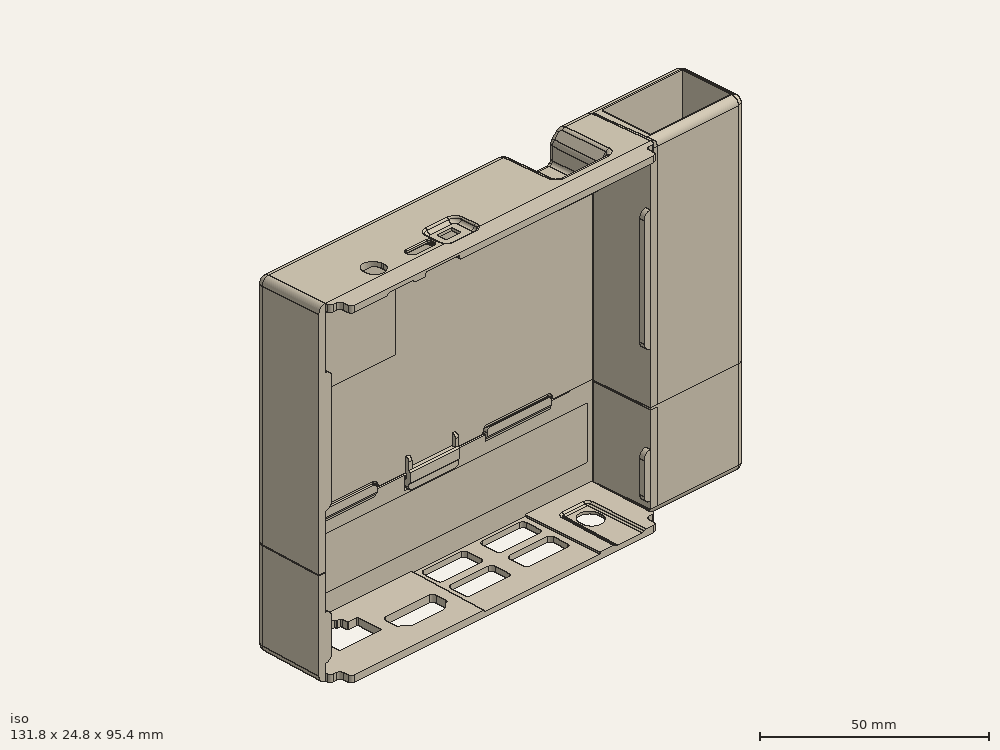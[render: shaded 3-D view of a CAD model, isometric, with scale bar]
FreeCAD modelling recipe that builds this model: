
FCSTD DOCUMENT  (FreeCAD 0.20R29177 +233 (Git))
Label: N2Case_10_12_2022
License: All rights reserved
LicenseURL: http://en.wikipedia.org/wiki/All_rights_reserved
objects: Part::Box×22, Part::Cylinder×11, Part::MultiFuse×9, Part::Cut×9, Part::Sphere×4, Part::Feature×2, Sketcher::SketchObject×2, PartDesign::Pad×2, PartDesign::Body×2
note: 65 computed .brp shape members not serialized (recipe doc carries the construction recipe); baked Part::Feature solids carry a one-line shape summary decoded from their .brp

FEATURE [Part::Feature] Solid  label="N2_BOTTOM_COVER"
  shape: bbox 104.6 x 25.21 x 71.78 mm, 343 faces (baked)
FEATURE [Part::Feature] Solid001  label="N2_TOP_COVER"
  shape: bbox 104.6 x 24.81 x 29.22 mm, 349 faces (baked)
FEATURE [Part::Box] Box  label="Cube"
  AttacherType = Attacher::AttachEngine3D
  Height = 15
  Length = 62.5
  Placement = pos=(-49,18,44) rot=(0,-1,0;4.71239rad)
  Width = 2
FEATURE [Part::MultiFuse] Fusion  label="BottomCover"
  Shapes = -> [Solid,Box]
FEATURE [Part::Box] Box001  label="Cube001"
  AttacherType = Attacher::AttachEngine3D
  Height = 15
  Length = 97.5
  Placement = pos=(48.5,20,-3.5) rot=(0,1,0;3.14159rad)
  Width = 2
FEATURE [Part::Cut] Cut
  Base = -> Fusion
  Tool = -> Box001
FEATURE [Part::Box] Box002  label="usbEthernet"
  AttacherType = Attacher::AttachEngine3D
  Height = 25
  Length = 72
  Placement = pos=(52.5,2.6,47.4) rot=(0,1,0;1.5708rad)
  Width = 15
FEATURE [Part::Box] Box003  label="usbEthernetCover"
  AttacherType = Attacher::AttachEngine3D
  Height = 27.5
  Length = 72
  Placement = pos=(50.5,2.2,47.4) rot=(0,1,0;1.5708rad)
  Width = 15.85
FEATURE [Part::Box] Box004  label="usbEthernetCover001"
  AttacherType = Attacher::AttachEngine3D
  Height = 27.52
  Length = 65.19
  Placement = pos=(49.98,17.6,45.39) rot=(0,1,0;1.5708rad)
  Width = 2.4
FEATURE [Part::Box] Box005  label="usbEthernetCover002"
  AttacherType = Attacher::AttachEngine3D
  Height = 2
  Length = 65.19
  Placement = pos=(77.5,2.2,45.39) rot=(0,1,0;1.5708rad)
  Width = 15.8
FEATURE [Part::Cylinder] Cylinder
  Angle = 90
  AttacherType = Attacher::AttachEngine3D
  FirstAngle = 0
  Height = 65.2
  Placement = pos=(77.5,2.2,-19.8) rot=(0,0,1;4.71239rad)
  Radius = 2
  SecondAngle = 0
FEATURE [Part::Cylinder] Cylinder001
  Angle = 90
  AttacherType = Attacher::AttachEngine3D
  FirstAngle = 0
  Height = 27.5
  Placement = pos=(77.5,18,45.4) rot=(0,1,0;4.71239rad)
  Radius = 2
  SecondAngle = 0
FEATURE [Part::Cylinder] Cylinder002
  Angle = 90
  AttacherType = Attacher::AttachEngine3D
  FirstAngle = 0
  Height = 15.8
  Placement = pos=(77.5,2.2,45.4) rot=(0.57735,0.57735,0.57735;4.18879rad)
  Radius = 2
  SecondAngle = 0
FEATURE [Part::Cylinder] Cylinder003
  Angle = 90
  AttacherType = Attacher::AttachEngine3D
  FirstAngle = 0
  Height = 65.2
  Placement = pos=(77.5,18,-19.8) rot=(0,0,1;0rad)
  Radius = 2
  SecondAngle = 0
FEATURE [Part::Box] Box006  label="usbEthernetCover003"
  AttacherType = Attacher::AttachEngine3D
  Height = 27.2
  Length = 65.19
  Placement = pos=(50.3,0.2,45.39) rot=(0,1,0;1.5708rad)
  Width = 2.4
FEATURE [Part::Cylinder] Cylinder004
  Angle = 90
  AttacherType = Attacher::AttachEngine3D
  FirstAngle = 0
  Height = 26.4
  Placement = pos=(77.5,2.2,45.4) rot=(-0.57735,0.57735,0.57735;4.18879rad)
  Radius = 2
  SecondAngle = 0
FEATURE [Part::Sphere] Sphere
  Angle1 = -90
  Angle2 = 90
  Angle3 = 360
  AttacherType = Attacher::AttachEngine3D
  Placement = pos=(77.5,18,45.4) rot=(0,0,1;0rad)
  Radius = 2
FEATURE [Part::Sphere] Sphere001
  Angle1 = -90
  Angle2 = 90
  Angle3 = 360
  AttacherType = Attacher::AttachEngine3D
  Placement = pos=(77.5,2.2,45.4) rot=(0,0,1;0rad)
  Radius = 2
FEATURE [Part::MultiFuse] Fusion001  label="usbCover"
  Shapes = -> [Box003,Box004,Box005,Cylinder,Cylinder001,Cylinder002,Cylinder003,Box006,Cylinder004,Sphere,Sphere001]
FEATURE [Part::MultiFuse] Fusion002
  Shapes = -> [Cut,Fusion001]
FEATURE [Part::Cut] Cut001  label="front"
  Base = -> Fusion002
  Tool = -> Box002
FEATURE [Part::Box] Box007  label="Cube002"
  AttacherType = Attacher::AttachEngine3D
  Height = 10
  Length = 30
  Placement = pos=(79.5,0,-19.8) rot=(0,1,0;3.14159rad)
  Width = 20
FEATURE [Part::Cut] Cut002
  Base = -> Cut001
  Tool = -> Box007
FEATURE [Part::Box] Box008  label="Cube003"
  AttacherType = Attacher::AttachEngine3D
  Height = 10
  Length = 30
  Placement = pos=(79.5,0,-19.8) rot=(0,1,0;3.14159rad)
  Width = 20
FEATURE [Part::Cut] Cut003  label="front001"
  Base = -> Cut002
  Tool = -> Box008
FEATURE [Part::Box] Box009  label="usbEthernet001"
  AttacherType = Attacher::AttachEngine3D
  Height = 25
  Length = 72
  Placement = pos=(52.5,2.6,6.3) rot=(0,1,0;1.5708rad)
  Width = 15
FEATURE [Part::Box] Box010  label="usbEthernetCover004"
  AttacherType = Attacher::AttachEngine3D
  Height = 27.5
  Length = 72
  Placement = pos=(50.5,2.2,-19.8) rot=(0,1,0;1.5708rad)
  Width = 15.85
FEATURE [Part::Box] Box011  label="usbEthernetCover005"
  AttacherType = Attacher::AttachEngine3D
  Height = 27.52
  Length = 65.19
  Placement = pos=(49.98,17.6,-19.8) rot=(0,1,0;1.5708rad)
  Width = 2.4
FEATURE [Part::Box] Box012  label="usbEthernetCover006"
  AttacherType = Attacher::AttachEngine3D
  Height = 2
  Length = 65.19
  Placement = pos=(77.5,2.2,-19.8) rot=(0,1,0;1.5708rad)
  Width = 15.8
FEATURE [Part::Box] Box013  label="usbEthernetCover007"
  AttacherType = Attacher::AttachEngine3D
  Height = 27.2
  Length = 65.19
  Placement = pos=(50.3,0.2,-19.8) rot=(0,1,0;1.5708rad)
  Width = 2.4
FEATURE [Part::Box] Box016  label="Cube005"
  AttacherType = Attacher::AttachEngine3D
  Height = 50
  Length = 29.5
  Placement = pos=(79.5,0,-45.4) rot=(0,1,0;3.14159rad)
  Width = 20
FEATURE [Part::MultiFuse] Fusion003
  Shapes = -> [Solid001,Box010,Box011,Box012,Box013]
FEATURE [Part::Cut] Cut004
  Base = -> Fusion003
  Tool = -> Box016
FEATURE [Part::Cut] Cut005
  Base = -> Cut004
  Tool = -> Box009
FEATURE [Part::Box] Box017  label="Cube006"
  AttacherType = Attacher::AttachEngine3D
  Height = 50
  Length = 23.5
  Placement = pos=(73.4,17.6,-45.39) rot=(0,1,0;3.14159rad)
  Width = 20
FEATURE [Part::Cut] Cut006
  Base = -> Cut005
  Tool = -> Box017
FEATURE [Part::Cylinder] Cylinder005
  Angle = 90
  AttacherType = Attacher::AttachEngine3D
  FirstAngle = 0
  Height = 65.2
  Placement = pos=(77.5,2.2,-45.4) rot=(0,0,-1;1.5708rad)
  Radius = 2
  SecondAngle = 0
FEATURE [Part::Cylinder] Cylinder006
  Angle = 90
  AttacherType = Attacher::AttachEngine3D
  FirstAngle = 0
  Height = 27.5
  Placement = pos=(77.5,18,-45.4) rot=(0,-1,0;1.5708rad)
  Radius = 2
  SecondAngle = 0
FEATURE [Part::Cylinder] Cylinder007
  Angle = 90
  AttacherType = Attacher::AttachEngine3D
  FirstAngle = 0
  Height = 15.8
  Placement = pos=(77.5,2.2,-45.4) rot=(-1,0,0;1.5708rad)
  Radius = 2
  SecondAngle = 0
FEATURE [Part::Cylinder] Cylinder008
  Angle = 90
  AttacherType = Attacher::AttachEngine3D
  FirstAngle = 0
  Height = 65.2
  Placement = pos=(77.5,18,-45.4) rot=(0,0,1;0rad)
  Radius = 2
  SecondAngle = 0
FEATURE [Part::Cylinder] Cylinder009
  Angle = 90
  AttacherType = Attacher::AttachEngine3D
  FirstAngle = 0
  Height = 27.6
  Placement = pos=(77.5,2.2,-45.4) rot=(-0.707107,0,0.707107;3.14159rad)
  Radius = 2
  SecondAngle = 0
FEATURE [Part::Cylinder] Cylinder010
  Angle = 90
  AttacherType = Attacher::AttachEngine3D
  FirstAngle = 0
  Height = 27.6
  Placement = pos=(77.5,18,-45.4) rot=(-0.57735,-0.57735,0.57735;2.0944rad)
  Radius = 2
  SecondAngle = 0
FEATURE [Part::Box] Box018  label="Cube007"
  AttacherType = Attacher::AttachEngine3D
  Height = 2
  Length = 27.6
  Placement = pos=(49.9,18,-45.4) rot=(1,0,0;3.14159rad)
  Width = 15.8
FEATURE [Part::Box] Box019  label="usbEthernet002"
  AttacherType = Attacher::AttachEngine3D
  Height = 25
  Length = 72
  Placement = pos=(52.5,2.6,-2.5) rot=(0,1,0;1.5708rad)
  Width = 15
FEATURE [Part::Sphere] Sphere002
  Angle1 = -90
  Angle2 = 90
  Angle3 = 360
  AttacherType = Attacher::AttachEngine3D
  Placement = pos=(77.5,18,-45.4) rot=(0,0,1;0rad)
  Radius = 2
FEATURE [Part::Sphere] Sphere003
  Angle1 = -90
  Angle2 = 90
  Angle3 = 360
  AttacherType = Attacher::AttachEngine3D
  Placement = pos=(77.5,2.2,-45.4) rot=(0,0,1;0rad)
  Radius = 2
FEATURE [Part::Box] Box020  label="Cube008"
  AttacherType = Attacher::AttachEngine3D
  Height = 40
  Length = 10
  Placement = pos=(73.6,0,-19.8) rot=(0,0,1;0rad)
  Width = 22
FEATURE [Part::MultiFuse] Fusion004  label="cuts"
  Shapes = -> [Box020,Box019]
FEATURE [Part::MultiFuse] Fusion005
  Shapes = -> [Sphere003,Cut006,Cylinder005,Cylinder006,Cylinder007,Cylinder008,Cylinder009,Cylinder010,Box018,Sphere002]
FEATURE [Part::Cut] Cut007  label="back"
  Base = -> Fusion005
  Tool = -> Fusion004
FEATURE [Part::Box] Box021  label="Cube009"
  AttacherType = Attacher::AttachEngine3D
  Height = 15
  Length = 97.5
  Placement = pos=(48.5,18,-25.1) rot=(0,1,0;3.14159rad)
  Width = 2
FEATURE [Part::MultiFuse] Fusion006  label="back001"
  Shapes = -> [Cut007,Box021]
FEATURE [Part::Box] Box068  label="logoBase001"
  AttacherType = Attacher::AttachEngine3D
  Height = 30
  Length = 35
  Placement = pos=(21.5,-44,15.25) rot=(0,0,1;0rad)
  Width = 1.8
FEATURE [Sketcher::SketchObject] Sketch001
  FullyConstrained = false
  MapMode = 5
  Support = -> [XY_Plane001]
  sketch-geometry (205):
    g0: LineSegment StartX=-15.0667 StartY=-2.9879 StartZ=0 EndX=-14.4175 EndY=-3.20194 EndZ=0
    g1: LineSegment StartX=-14.1386 StartY=-3.3581 StartZ=0 EndX=-13.8673 EndY=-3.55064 EndZ=0
    g2: LineSegment StartX=-10.8098 StartY=-4.00788 StartZ=0 EndX=-10.5716 EndY=-4.29909 EndZ=0
    g3: LineSegment StartX=-10.5716 StartY=-4.29909 StartZ=0 EndX=-10.1338 EndY=-4.33136 EndZ=0
    g4: LineSegment StartX=-10.1338 StartY=-4.33136 StartZ=0 EndX=-9.89036 EndY=-4.3898 EndZ=0
    g5: LineSegment StartX=-9.51656 StartY=-5.73022 StartZ=0 EndX=-9.24931 EndY=-5.76229 EndZ=0
    g6: LineSegment StartX=-9.24931 StartY=-5.76229 StartZ=0 EndX=-8.92861 EndY=-5.90126 EndZ=0
    g7: LineSegment StartX=-8.92861 StartY=-5.90126 StartZ=0 EndX=-8.54378 EndY=-5.86384 EndZ=0
    g8: LineSegment StartX=-8.54378 StartY=-5.86384 StartZ=0 EndX=-7.71788 EndY=-5.75845 EndZ=0
    g9: LineSegment StartX=-7.71788 StartY=-5.75845 StartZ=0 EndX=-7.37291 EndY=-5.97257 EndZ=0
    g10: LineSegment StartX=-7.37291 StartY=-5.97257 StartZ=0 EndX=-6.72487 EndY=-5.72038 EndZ=0
    g11: LineSegment StartX=-6.72487 StartY=-5.72038 StartZ=0 EndX=-6.27066 EndY=-5.69481 EndZ=0
    g12: LineSegment StartX=-6.27066 StartY=-5.69481 StartZ=0 EndX=-6.06223 EndY=-5.80493 EndZ=0
    g13: LineSegment StartX=-6.06223 StartY=-5.80493 StartZ=0 EndX=-5.35089 EndY=-5.48914 EndZ=0
    g14: LineSegment StartX=-5.35089 StartY=-5.48914 StartZ=0 EndX=-5.02402 EndY=-5.48914 EndZ=0
    g15: LineSegment StartX=-5.02402 StartY=-5.48914 StartZ=0 EndX=-4.80126 EndY=-5.53132 EndZ=0
    g16: LineSegment StartX=-4.80126 StartY=-5.53132 StartZ=0 EndX=-4.19735 EndY=-5.16248 EndZ=0
    g17: LineSegment StartX=-3.75191 StartY=-4.97251 StartZ=0 EndX=-3.37714 EndY=-4.97251 EndZ=0
    g18: LineSegment StartX=-3.37714 StartY=-4.97251 StartZ=0 EndX=-2.81898 EndY=-4.45422 EndZ=0
    g19: LineSegment StartX=-2.81898 StartY=-4.45422 StartZ=0 EndX=-2.62761 EndY=-4.34259 EndZ=0
    g20: LineSegment StartX=-2.62761 StartY=-4.34259 StartZ=0 EndX=-2.15112 EndY=-4.35765 EndZ=0
    g21: LineSegment StartX=-2.38042 StartY=-4.51801 StartZ=0 EndX=-3.18577 EndY=-5.42702 EndZ=0
    g22: LineSegment StartX=-3.18577 StartY=-5.42702 StartZ=0 EndX=-3.61318 EndY=-6.05824 EndZ=0
    g23: LineSegment StartX=-3.61318 StartY=-6.05824 StartZ=0 EndX=-3.7111 EndY=-6.64579 EndZ=0
    g24: LineSegment StartX=-3.7111 StartY=-6.64579 StartZ=0 EndX=-3.83514 EndY=-7.15501 EndZ=0
    g25: LineSegment StartX=-3.83514 StartY=-7.15501 StartZ=0 EndX=-3.75878 EndY=-7.50876 EndZ=0
    g26: LineSegment StartX=-3.75878 StartY=-7.50876 StartZ=0 EndX=-3.70596 EndY=-7.68135 EndZ=0
    g27: LineSegment StartX=-3.70596 StartY=-7.68135 StartZ=0 EndX=-3.53967 EndY=-7.85202 EndZ=0
    g28: LineSegment StartX=-3.53967 StartY=-7.85202 StartZ=0 EndX=-3.4685 EndY=-8.65617 EndZ=0
    g29: LineSegment StartX=-3.27268 StartY=-8.56671 StartZ=0 EndX=-3.16823 EndY=-8.76909 EndZ=0
    g30: LineSegment StartX=-3.07088 StartY=-9.32083 StartZ=0 EndX=-2.84207 EndY=-9.3355 EndZ=0
    g31: LineSegment StartX=-2.84207 StartY=-9.3355 StartZ=0 EndX=-2.45193 EndY=-10.0982 EndZ=0
    g32: LineSegment StartX=-2.45193 StartY=-10.0982 StartZ=0 EndX=-2.24953 EndY=-10.1304 EndZ=0
    g33: LineSegment StartX=-2.24953 StartY=-10.1304 StartZ=0 EndX=-0.96042 EndY=-11.8753 EndZ=0
    g34: LineSegment StartX=-0.96042 StartY=-11.8753 StartZ=0 EndX=-0.153326 EndY=-11.3889 EndZ=0
    g35: LineSegment StartX=-0.153326 StartY=-11.3889 StartZ=0 EndX=0.461347 EndY=-10.7689 EndZ=0
    g36: LineSegment StartX=0.461347 StartY=-10.7689 StartZ=0 EndX=0.669802 EndY=-10.7261 EndZ=0
    g37: LineSegment StartX=0.669802 StartY=-10.7261 StartZ=0 EndX=1.31724 EndY=-9.70998 EndZ=0
    g38: LineSegment StartX=1.31724 StartY=-9.70998 StartZ=0 EndX=1.51826 EndY=-9.65081 EndZ=0
    g39: LineSegment StartX=1.51826 StartY=-9.65081 StartZ=0 EndX=1.74022 EndY=-9.08937 EndZ=0
    g40: LineSegment StartX=1.74022 StartY=-9.08937 StartZ=0 EndX=2.02094 EndY=-9.04367 EndZ=0
    g41: LineSegment StartX=2.02094 StartY=-9.04367 StartZ=0 EndX=2.39306 EndY=-7.80327 EndZ=0
    g42: LineSegment StartX=2.39306 StartY=-7.80327 StartZ=0 EndX=2.58839 EndY=-7.69871 EndZ=0
    g43: LineSegment StartX=2.6542 StartY=-7.03945 StartZ=0 EndX=2.86963 EndY=-6.81749 EndZ=0
    g44: LineSegment StartX=2.86963 StartY=-6.81749 StartZ=0 EndX=3.0916 EndY=-6.92847 EndZ=0
    g45: LineSegment StartX=3.0916 StartY=-6.92847 StartZ=0 EndX=3.79666 EndY=-7.57478 EndZ=0
    g46: LineSegment StartX=3.79666 StartY=-7.57478 StartZ=0 EndX=3.93376 EndY=-7.50297 EndZ=0
    g47: LineSegment StartX=3.93376 StartY=-7.50297 StartZ=0 EndX=4.46256 EndY=-7.97301 EndZ=0
    g48: LineSegment StartX=4.46256 StartY=-7.97301 StartZ=0 EndX=4.68452 EndY=-7.92079 EndZ=0
    g49: LineSegment StartX=4.68452 StartY=-7.92079 StartZ=0 EndX=5.1154 EndY=-8.34513 EndZ=0
    g50: LineSegment StartX=5.1154 StartY=-8.34513 StartZ=0 EndX=5.32431 EndY=-8.28637 EndZ=0
    g51: LineSegment StartX=5.32431 StartY=-8.28637 StartZ=0 EndX=6.23668 EndY=-8.79564 EndZ=0
    g52: LineSegment StartX=6.23668 StartY=-8.79564 StartZ=0 EndX=6.50362 EndY=-8.76631 EndZ=0
    g53: LineSegment StartX=6.50362 StartY=-8.76631 StartZ=0 EndX=7.14802 EndY=-9.05537 EndZ=0
    g54: LineSegment StartX=7.14802 StartY=-9.05537 StartZ=0 EndX=8.04883 EndY=-9.18613 EndZ=0
    g55: LineSegment StartX=8.04883 StartY=-9.18613 StartZ=0 EndX=8.36847 EndY=-7.93662 EndZ=0
    g56: LineSegment StartX=8.36847 StartY=-7.93662 StartZ=0 EndX=8.49923 EndY=-7.79133 EndZ=0
    g57: LineSegment StartX=8.49923 StartY=-7.79133 StartZ=0 EndX=8.43477 EndY=-6.72206 EndZ=0
    g58: LineSegment StartX=8.43477 StartY=-6.72206 StartZ=0 EndX=8.58621 EndY=-6.47988 EndZ=0
    g59: LineSegment StartX=8.58621 StartY=-6.47988 StartZ=0 EndX=8.32296 EndY=-5.53178 EndZ=0
    g60: LineSegment StartX=8.32296 StartY=-5.53178 StartZ=0 EndX=8.43984 EndY=-5.19091 EndZ=0
    g61: LineSegment StartX=8.43984 StartY=-5.19091 StartZ=0 EndX=8.07426 EndY=-4.39307 EndZ=0
    g62: LineSegment StartX=8.07426 StartY=-4.39307 StartZ=0 EndX=8.04236 EndY=-4.17777 EndZ=0
    g63: LineSegment StartX=8.04236 StartY=-4.17777 StartZ=0 EndX=8.0902 EndY=-3.99438 EndZ=0
    g64: LineSegment StartX=8.4103 StartY=-4.11103 StartZ=0 EndX=8.72013 EndY=-4.0502 EndZ=0
    g65: LineSegment StartX=8.72013 StartY=-4.0502 StartZ=0 EndX=9.31817 EndY=-4.0502 EndZ=0
    g66: LineSegment StartX=9.31817 StartY=-4.0502 StartZ=0 EndX=9.82964 EndY=-4.15887 EndZ=0
    g67: LineSegment StartX=10.1326 StartY=-3.9675 StartZ=0 EndX=10.5175 EndY=-3.9623 EndZ=0
    g68: LineSegment StartX=10.5175 StartY=-3.9623 StartZ=0 EndX=10.8831 EndY=-3.97536 EndZ=0
    g69: LineSegment StartX=10.8831 StartY=-3.97536 StartZ=0 EndX=11.2245 EndY=-4.09431 EndZ=0
    g70: LineSegment StartX=11.2245 StartY=-4.09431 StartZ=0 EndX=11.6861 EndY=-3.91007 EndZ=0
    g71: LineSegment StartX=11.6861 StartY=-3.91007 StartZ=0 EndX=12.1039 EndY=-3.88396 EndZ=0
    g72: LineSegment StartX=12.1039 StartY=-3.88396 StartZ=0 EndX=12.6 EndY=-3.9623 EndZ=0
    g73: LineSegment StartX=12.6 StartY=-3.9623 StartZ=0 EndX=13.5793 EndY=-3.87743 EndZ=0
    g74: LineSegment StartX=13.5793 StartY=-3.87743 StartZ=0 EndX=14.3888 EndY=-3.74687 EndZ=0
    g75: LineSegment StartX=14.3888 StartY=-3.74687 StartZ=0 EndX=14.7544 EndY=-3.68158 EndZ=0
    g76: LineSegment StartX=14.7544 StartY=-3.68158 StartZ=0 EndX=15.2767 EndY=-3.75339 EndZ=0
    g77: LineSegment StartX=15.2767 StartY=-3.75339 StartZ=0 EndX=15.0432 EndY=-3.24137 EndZ=0
    g78: LineSegment StartX=15.0432 StartY=-3.24137 StartZ=0 EndX=14.5209 EndY=-2.51672 EndZ=0
    g79: LineSegment StartX=14.5209 StartY=-2.51672 StartZ=0 EndX=14.0378 EndY=-1.99445 EndZ=0
    g80: LineSegment StartX=14.0378 StartY=-1.99445 StartZ=0 EndX=13.2802 EndY=-1.54625 EndZ=0
    g81: LineSegment StartX=13.2802 StartY=-1.54625 StartZ=0 EndX=13.0438 EndY=-1.23117 EndZ=0
    g82: LineSegment StartX=13.0438 StartY=-1.23117 StartZ=0 EndX=12.1074 EndY=-0.797939 EndZ=0
    g83: LineSegment StartX=12.1074 StartY=-0.797939 StartZ=0 EndX=11.3804 EndY=-0.250878 EndZ=0
    g84: LineSegment StartX=11.3804 StartY=-0.250878 StartZ=0 EndX=10.4396 EndY=0.304889 EndZ=0
    g85: LineSegment StartX=10.4396 StartY=0.304889 StartZ=0 EndX=9.59526 EndY=0.727998 EndZ=0
    g86: LineSegment StartX=9.59526 StartY=0.727998 StartZ=0 EndX=8.53624 EndY=0.97306 EndZ=0
    g87: LineSegment StartX=8.53624 StartY=0.97306 StartZ=0 EndX=7.199 EndY=0.97306 EndZ=0
    g88: LineSegment StartX=7.199 StartY=0.97306 StartZ=0 EndX=5.77932 EndY=0.795578 EndZ=0
    g89: LineSegment StartX=5.77932 StartY=0.795578 StartZ=0 EndX=5.60186 EndY=0.795578 EndZ=0
    g90: LineSegment StartX=5.60186 StartY=0.795578 StartZ=0 EndX=5.83178 EndY=0.981815 EndZ=0
    g91: LineSegment StartX=5.83178 StartY=0.981815 StartZ=0 EndX=6.25403 EndY=1.1582 EndZ=0
    g92: LineSegment StartX=6.30214 StartY=1.38269 StartZ=0 EndX=7.17987 EndY=1.70686 EndZ=0
    g93: LineSegment StartX=7.17987 StartY=1.70686 StartZ=0 EndX=7.44682 EndY=1.79438 EndZ=0
    g94: LineSegment StartX=7.44682 StartY=1.79438 StartZ=0 EndX=7.49058 EndY=2.12696 EndZ=0
    g95: LineSegment StartX=7.49058 StartY=2.12696 StartZ=0 EndX=8.30058 EndY=2.66839 EndZ=0
    g96: LineSegment StartX=8.30058 StartY=2.66839 StartZ=0 EndX=8.68575 EndY=2.81854 EndZ=0
    g97: LineSegment StartX=8.68575 StartY=2.81854 StartZ=0 EndX=8.68575 EndY=3.12537 EndZ=0
    g98: LineSegment StartX=8.68575 StartY=3.12537 StartZ=0 EndX=8.89508 EndY=3.18684 EndZ=0
    g99: LineSegment StartX=8.89508 StartY=3.18684 StartZ=0 EndX=9.63492 EndY=4.06602 EndZ=0
    g100: LineSegment StartX=9.63492 StartY=4.06602 StartZ=0 EndX=9.62638 EndY=4.32743 EndZ=0
    g101: LineSegment StartX=9.62638 StartY=4.32743 StartZ=0 EndX=10.2068 EndY=5.18314 EndZ=0
    g102: LineSegment StartX=10.2068 StartY=5.18314 StartZ=0 EndX=9.25518 EndY=5.64445 EndZ=0
    g103: LineSegment StartX=9.1102 StartY=5.87597 StartZ=0 EndX=8.32132 EndY=5.97336 EndZ=0
    g104: LineSegment StartX=8.32132 StartY=5.97336 StartZ=0 EndX=8.15466 EndY=6.06625 EndZ=0
    g105: LineSegment StartX=7.63471 StartY=6.13088 StartZ=0 EndX=7.56391 EndY=6.33267 EndZ=0
    g106: LineSegment StartX=7.56391 StartY=6.33267 StartZ=0 EndX=6.74832 EndY=6.35496 EndZ=0
    g107: LineSegment StartX=6.74832 StartY=6.35496 StartZ=0 EndX=6.46819 EndY=6.29526 EndZ=0
    g108: LineSegment StartX=6.46819 StartY=6.29526 StartZ=0 EndX=6.27042 EndY=6.61061 EndZ=0
    g109: LineSegment StartX=6.27042 StartY=6.61061 StartZ=0 EndX=5.40453 EndY=6.33267 EndZ=0
    g110: LineSegment StartX=5.40453 StartY=6.33267 StartZ=0 EndX=5.27091 EndY=6.47164 EndZ=0
    g111: LineSegment StartX=5.27091 StartY=6.47164 StartZ=0 EndX=4.56942 EndY=6.24725 EndZ=0
    g112: LineSegment StartX=4.56942 StartY=6.24725 StartZ=0 EndX=4.44161 EndY=6.40652 EndZ=0
    g113: LineSegment StartX=4.44161 StartY=6.40652 StartZ=0 EndX=3.4195 EndY=5.94588 EndZ=0
    g114: LineSegment StartX=3.4195 StartY=5.94588 StartZ=0 EndX=3.29192 EndY=6.1532 EndZ=0
    g115: LineSegment StartX=3.29192 StartY=6.1532 StartZ=0 EndX=2.15964 EndY=5.49137 EndZ=0
    g116: LineSegment StartX=2.15964 StartY=5.49137 StartZ=0 EndX=2.00016 EndY=5.69869 EndZ=0
    g117: LineSegment StartX=2.00016 StartY=5.69869 StartZ=0 EndX=1.6185 EndY=5.34828 EndZ=0
    g118: LineSegment StartX=1.6185 StartY=5.34828 StartZ=0 EndX=1.45984 EndY=5.94974 EndZ=0
    g119: LineSegment StartX=1.38165 StartY=6.28651 StartZ=0 EndX=1.14534 EndY=6.29963 EndZ=0
    g120: LineSegment StartX=0.348522 StartY=7.29544 StartZ=0 EndX=0.126706 EndY=7.68126 EndZ=0
    g121: LineSegment StartX=0.126706 StartY=7.68126 StartZ=0 EndX=-0.415308 EndY=8.18163 EndZ=0
    g122: LineSegment StartX=-0.415308 StartY=8.18163 StartZ=0 EndX=-0.872658 EndY=8.6237 EndZ=0
    g123: LineSegment StartX=-0.872658 StartY=8.6237 StartZ=0 EndX=-1.12074 EndY=8.64329 EndZ=0
    g124: LineSegment StartX=-1.12074 StartY=8.64329 StartZ=0 EndX=-1.79316 EndY=9.11986 EndZ=0
    g125: LineSegment StartX=-1.79316 StartY=9.11986 StartZ=0 EndX=-2.31488 EndY=9.12122 EndZ=0
    g126: LineSegment StartX=-2.31488 StartY=9.12122 StartZ=0 EndX=-2.71321 EndY=9.13846 EndZ=0
    g127: LineSegment StartX=-2.71321 StartY=9.13846 StartZ=0 EndX=-2.88425 EndY=9.34157 EndZ=0
    g128: LineSegment StartX=-2.88425 StartY=9.34157 StartZ=0 EndX=-3.16779 EndY=9.26454 EndZ=0
    g129: LineSegment StartX=-3.70739 StartY=9.82796 StartZ=0 EndX=-4.04915 EndY=9.7003 EndZ=0
    g130: LineSegment StartX=-4.04915 StartY=9.7003 StartZ=0 EndX=-4.42988 EndY=10.011 EndZ=0
    g131: LineSegment StartX=-5.98947 StartY=10.3656 StartZ=0 EndX=-7.32605 EndY=10.4108 EndZ=0
    g132: LineSegment StartX=-7.25254 StartY=9.13254 StartZ=0 EndX=-7.36878 EndY=8.7693 EndZ=0
    g133: LineSegment StartX=-7.36878 StartY=8.7693 StartZ=0 EndX=-7.2614 EndY=7.83762 EndZ=0
    g134: LineSegment StartX=-7.2614 StartY=7.83762 StartZ=0 EndX=-7.41112 EndY=7.6042 EndZ=0
    g135: LineSegment StartX=-7.41112 StartY=7.6042 StartZ=0 EndX=-7.09216 EndY=6.74302 EndZ=0
    g136: LineSegment StartX=-7.09216 StartY=6.74302 StartZ=0 EndX=-7.10014 EndY=6.55962 EndZ=0
    g137: LineSegment StartX=-7.10014 StartY=6.55962 StartZ=0 EndX=-7.29151 EndY=6.3842 EndZ=0
    g138: LineSegment StartX=-7.29151 StartY=6.3842 StartZ=0 EndX=-6.74132 EndY=5.29976 EndZ=0
    g139: LineSegment StartX=-6.74132 StartY=5.29976 StartZ=0 EndX=-6.87495 EndY=5.02732 EndZ=0
    g140: LineSegment StartX=-6.87495 StartY=5.02732 StartZ=0 EndX=-6.31586 EndY=4.42065 EndZ=0
    g141: LineSegment StartX=-6.31586 StartY=4.42065 StartZ=0 EndX=-6.30396 EndY=4.19463 EndZ=0
    g142: LineSegment StartX=-6.30396 StartY=4.19463 StartZ=0 EndX=-6.05415 EndY=4.0043 EndZ=0
    g143: LineSegment StartX=-6.05415 StartY=4.0043 StartZ=0 EndX=-6.18501 EndY=3.95672 EndZ=0
    g144: LineSegment StartX=-6.18501 StartY=3.95672 StartZ=0 EndX=-5.54265 EndY=3.07645 EndZ=0
    g145: LineSegment StartX=-5.54265 StartY=3.07645 StartZ=0 EndX=-5.57833 EndY=2.90991 EndZ=0
    g146: LineSegment StartX=-5.57833 StartY=2.90991 StartZ=0 EndX=-5.1263 EndY=2.41029 EndZ=0
    g147: LineSegment StartX=-5.1263 StartY=2.41029 StartZ=0 EndX=-5.18578 EndY=2.26755 EndZ=0
    g148: LineSegment StartX=-5.18578 StartY=2.26755 StartZ=0 EndX=-4.73375 EndY=1.89878 EndZ=0
    g149: LineSegment StartX=-4.73375 StartY=1.89878 StartZ=0 EndX=-4.42446 EndY=1.5895 EndZ=0
    g150: LineSegment StartX=-4.42446 StartY=1.5895 StartZ=0 EndX=-5.31663 EndY=1.29211 EndZ=0
    g151: LineSegment StartX=-5.31663 StartY=1.29211 StartZ=0 EndX=-5.84004 EndY=1.08988 EndZ=0
    g152: LineSegment StartX=-5.84004 StartY=1.08988 StartZ=0 EndX=-6.04226 EndY=0.792495 EndZ=0
    g153: LineSegment StartX=-6.04226 StartY=0.792495 StartZ=0 EndX=-6.94632 EndY=0.994719 EndZ=0
    g154: LineSegment StartX=-6.94632 StartY=0.994719 StartZ=0 EndX=-7.19613 EndY=0.887659 EndZ=0
    g155: LineSegment StartX=-7.19613 StartY=0.887659 StartZ=0 EndX=-7.8147 EndY=1.0423 EndZ=0
    g156: LineSegment StartX=-7.8147 StartY=1.0423 StartZ=0 EndX=-8.02502 EndY=0.969153 EndZ=0
    g157: LineSegment StartX=-8.02502 StartY=0.969153 StartZ=0 EndX=-8.60267 EndY=1.03042 EndZ=0
    g158: LineSegment StartX=-8.60267 StartY=1.03042 StartZ=0 EndX=-8.8346 EndY=0.872878 EndZ=0
    g159: LineSegment StartX=-8.8346 StartY=0.872878 StartZ=0 EndX=-9.33349 EndY=0.929767 EndZ=0
    g160: LineSegment StartX=-9.33349 StartY=0.929767 StartZ=0 EndX=-9.66169 EndY=0.649695 EndZ=0
    g161: LineSegment StartX=-9.66169 StartY=0.649695 StartZ=0 EndX=-10.3249 EndY=0.649695 EndZ=0
    g162: LineSegment StartX=-10.3249 StartY=0.649695 StartZ=0 EndX=-11.0107 EndY=0.32425 EndZ=0
    g163: LineSegment StartX=-11.0107 StartY=0.32425 StartZ=0 EndX=-11.7283 EndY=0.053139 EndZ=0
    g164: LineSegment StartX=-11.7283 StartY=0.053139 StartZ=0 EndX=-12.2971 EndY=-0.13161 EndZ=0
    g165: LineSegment StartX=-12.2971 StartY=-0.13161 StartZ=0 EndX=-12.4212 EndY=-0.347049 EndZ=0
    g166: LineSegment StartX=-12.4212 StartY=-0.347049 StartZ=0 EndX=-13.296 EndY=-0.817096 EndZ=0
    g167: LineSegment StartX=-13.296 StartY=-0.817096 StartZ=0 EndX=-13.9227 EndY=-1.24144 EndZ=0
    g168: LineSegment StartX=-13.9227 StartY=-1.24144 StartZ=0 EndX=-14.1708 EndY=-1.59398 EndZ=0
    g169: LineSegment StartX=-14.1708 StartY=-1.59398 StartZ=0 EndX=-14.5386 EndY=-2.09216 EndZ=0
    g170: LineSegment StartX=-14.5386 StartY=-2.09216 StartZ=0 EndX=-14.7831 EndY=-2.4577 EndZ=0
    g171: LineSegment StartX=-14.7831 StartY=-2.4577 StartZ=0 EndX=-15.0667 EndY=-2.9879 EndZ=0
    g172: LineSegment StartX=7.82861 StartY=6.04487 StartZ=0 EndX=7.63471 EndY=6.13088 EndZ=0
    g173: LineSegment StartX=-14.4175 StartY=-3.20194 StartZ=0 EndX=-14.1386 EndY=-3.3581 EndZ=0
    g174: LineSegment StartX=-13.8673 StartY=-3.55064 StartZ=0 EndX=-13.4107 EndY=-3.57136 EndZ=0
    g175: LineSegment StartX=-13.1321 StartY=-3.61699 StartZ=0 EndX=-12.817 EndY=-3.62343 EndZ=0
    g176: LineSegment StartX=-12.817 StartY=-3.62343 StartZ=0 EndX=-12.4662 EndY=-3.85302 EndZ=0
    g177: LineSegment StartX=-13.4107 StartY=-3.57136 StartZ=0 EndX=-13.1321 EndY=-3.61699 EndZ=0
    g178: LineSegment StartX=-12.4662 StartY=-3.85302 StartZ=0 EndX=-11.8704 EndY=-3.85302 EndZ=0
    g179: LineSegment StartX=-11.8704 StartY=-3.85302 StartZ=0 EndX=-11.5204 EndY=-4.00836 EndZ=0
    g180: LineSegment StartX=-11.5204 StartY=-4.00836 StartZ=0 EndX=-11.1389 EndY=-4.05555 EndZ=0
    g181: LineSegment StartX=-11.1389 StartY=-4.05555 StartZ=0 EndX=-10.8098 EndY=-4.00788 EndZ=0
    g182: LineSegment StartX=-9.89036 StartY=-4.3898 StartZ=0 EndX=-9.99555 EndY=-4.87697 EndZ=0
    g183: LineSegment StartX=-9.99555 StartY=-4.87697 StartZ=0 EndX=-10.0894 EndY=-5.36391 EndZ=0
    g184: LineSegment StartX=-10.0894 StartY=-5.36391 StartZ=0 EndX=-10.107 EndY=-5.50471 EndZ=0
    g185: LineSegment StartX=-10.107 StartY=-5.50471 StartZ=0 EndX=-9.77848 EndY=-5.63965 EndZ=0
    g186: LineSegment StartX=-9.77848 StartY=-5.63965 StartZ=0 EndX=-9.51656 EndY=-5.73022 EndZ=0
    g187: LineSegment StartX=-4.19735 StartY=-5.16248 StartZ=0 EndX=-3.75191 EndY=-4.97251 EndZ=0
    g188: LineSegment StartX=-2.38042 StartY=-4.51801 StartZ=0 EndX=-2.15112 EndY=-4.35765 EndZ=0
    g189: LineSegment StartX=-3.4685 StartY=-8.65617 StartZ=0 EndX=-3.27268 EndY=-8.56671 EndZ=0
    g190: LineSegment StartX=-3.16823 StartY=-8.76909 StartZ=0 EndX=-3.07088 EndY=-9.32083 EndZ=0
    g191: LineSegment StartX=2.58839 StartY=-7.69871 StartZ=0 EndX=2.6542 EndY=-7.03945 EndZ=0
    g192: LineSegment StartX=8.0902 StartY=-3.99438 StartZ=0 EndX=8.4103 EndY=-4.11103 EndZ=0
    g193: LineSegment StartX=9.82964 StartY=-4.15887 StartZ=0 EndX=10.1326 EndY=-3.9675 EndZ=0
    g194: LineSegment StartX=6.30214 StartY=1.38269 StartZ=0 EndX=6.25403 EndY=1.1582 EndZ=0
    g195: LineSegment StartX=1.38165 StartY=6.28651 StartZ=0 EndX=1.45984 EndY=5.94974 EndZ=0
    g196: LineSegment StartX=0.348522 StartY=7.29544 StartZ=0 EndX=0.824344 EndY=6.91479 EndZ=0
    g197: LineSegment StartX=0.824344 StartY=6.91479 StartZ=0 EndX=1.14534 EndY=6.29963 EndZ=0
    g198: LineSegment StartX=-3.70739 StartY=9.82796 StartZ=0 EndX=-3.16779 EndY=9.26454 EndZ=0
    g199: LineSegment StartX=-5.98947 StartY=10.3656 StartZ=0 EndX=-5.43038 EndY=10.4489 EndZ=0
    g200: LineSegment StartX=-5.43038 StartY=10.4489 StartZ=0 EndX=-4.9791 EndY=10.1425 EndZ=0
    g201: LineSegment StartX=-4.42988 StartY=10.011 StartZ=0 EndX=-4.9791 EndY=10.1425 EndZ=0
    g202: LineSegment StartX=-7.25254 StartY=9.13254 StartZ=0 EndX=-7.32605 EndY=10.4108 EndZ=0
    g203: LineSegment StartX=7.82861 StartY=6.04487 StartZ=0 EndX=8.15466 EndY=6.06625 EndZ=0
    g204: LineSegment StartX=9.1102 StartY=5.87597 StartZ=0 EndX=9.25518 EndY=5.64445 EndZ=0
  constraints (114):
    c: Coincident(g4,g3)
    c: Coincident(g6,g5)
    c: Coincident(g8,g7)
    c: Coincident(g9,g8)
    c: Coincident(g10,g9)
    c: Coincident(g11,g10)
    c: Coincident(g13,g12)
    c: Coincident(g16,g15)
    c: Coincident(g22,g21)
    c: Coincident(g25,g24)
    c: Coincident(g26,g25)
    c: Coincident(g28,g27)
    c: Coincident(g33,g32)
    c: Coincident(g37,g36)
    c: Coincident(g38,g37)
    c: Coincident(g40,g39)
    c: Coincident(g44,g43)
    c: Coincident(g51,g50)
    c: Coincident(g52,g51)
    c: Coincident(g57,g56)
    c: Coincident(g58,g57)
    c: Coincident(g59,g58)
    c: Coincident(g61,g60)
    c: Coincident(g63,g62)
    c: Coincident(g66,g65)
    c: Coincident(g70,g69)
    c: Coincident(g72,g71)
    c: Coincident(g73,g72)
    c: Coincident(g74,g73)
    c: Coincident(g77,g76)
    c: Coincident(g80,g79)
    c: Coincident(g81,g80)
    c: Coincident(g83,g82)
    c: Coincident(g85,g84)
    c: Coincident(g86,g85)
    c: Coincident(g87,g86)
    c: Coincident(g89,g88)
    c: Coincident(g90,g89)
    c: Coincident(g91,g90)
    c: Coincident(g93,g92)
    c: Coincident(g95,g94)
    c: Coincident(g97,g96)
    c: Coincident(g98,g97)
    c: Coincident(g99,g98)
    c: Coincident(g100,g99)
    c: Coincident(g104,g103)
    c: Coincident(g106,g105)
    c: Coincident(g107,g106)
    c: Coincident(g111,g110)
    c: Coincident(g113,g112)
    c: Coincident(g118,g117)
    c: Coincident(g122,g121)
    c: Coincident(g126,g125)
    c: Coincident(g130,g129)
    c: Coincident(g133,g132)
    c: Coincident(g134,g133)
    c: Coincident(g135,g134)
    c: Coincident(g139,g138)
    c: Coincident(g142,g141)
    c: Coincident(g156,g155)
    c: Coincident(g157,g156)
    c: Coincident(g159,g158)
    c: Coincident(g161,g160)
    c: Coincident(g164,g163)
    c: Coincident(g165,g164)
    c: Coincident(g168,g167)
    c: Coincident(g169,g168)
    c: Coincident(g171,g170)
    c: Coincident(g171,g0)
    c: Coincident(g172,g105)
    c: DistanceX(g165) = -12.4212
    c: DistanceY(g165) = -0.347049
    c: Coincident(g173,g0)
    c: Coincident(g173,g1)
    c: Coincident(g174,g1)
    c: Coincident(g177,g174)
    c: Coincident(g177,g175)
    c: Coincident(g178,g176)
    c: Coincident(g181,g2)
    c: Coincident(g182,g4)
    c: Coincident(g186,g185)
    c: Coincident(g186,g5)
    c: Coincident(g187,g16)
    c: Coincident(g187,g17)
    c: Coincident(g188,g21)
    c: Coincident(g188,g20)
    c: Coincident(g189,g28)
    c: Coincident(g189,g29)
    c: Coincident(g190,g29)
    c: Coincident(g190,g30)
    c: Coincident(g191,g42)
    c: Coincident(g191,g43)
    c: Coincident(g192,g63)
    c: Coincident(g192,g64)
    c: Coincident(g193,g66)
    c: Coincident(g193,g67)
    c: Coincident(g194,g92)
    c: Coincident(g194,g91)
    c: Coincident(g195,g119)
    c: Coincident(g195,g118)
    c: Coincident(g196,g120)
    c: Coincident(g197,g119)
    c: Coincident(g198,g129)
    c: Coincident(g198,g128)
    c: Coincident(g199,g131)
    c: Coincident(g200,g199)
    c: Coincident(g201,g130)
    c: Coincident(g201,g200)
    c: Coincident(g202,g132)
    c: Coincident(g202,g131)
    c: Coincident(g203,g172)
    c: Coincident(g203,g104)
    c: Coincident(g204,g103)
    c: Coincident(g204,g102)
FEATURE [PartDesign::Pad] Pad001
  Direction = (0,0,1)
  Length = 3
  Length2 = 10
  Profile = -> Sketch001
  ReferenceAxis = -> Sketch001 [N_Axis]
  Type = 0
FEATURE [PartDesign::Body] Body001  label="logo002"
  Group = -> [Sketch001,Pad001]
  Origin = -> Origin001
  Placement = pos=(39.35,-43,30) rot=(1,0,0;1.5708rad)
  Tip = -> Pad001
FEATURE [Part::MultiFuse] Fusion040  label="logo003"
  Placement = pos=(-69,-26,58) rot=(1,0,0;3.14159rad)
  Shapes = -> [Body001,Box068]
FEATURE [Part::Cut] Cut008  label="front002"
  Base = -> Cut003
  Tool = -> Fusion040
FEATURE [Part::Box] Box069  label="logoBase002"
  AttacherType = Attacher::AttachEngine3D
  Height = 30
  Length = 35
  Placement = pos=(21.5,-44,15.25) rot=(0,0,1;0rad)
  Width = 1.8
FEATURE [Sketcher::SketchObject] Sketch002
  FullyConstrained = false
  MapMode = 5
  Support = -> [XY_Plane002]
  sketch-geometry (205):
    g0: LineSegment StartX=-15.0667 StartY=-2.9879 StartZ=0 EndX=-14.4175 EndY=-3.20194 EndZ=0
    g1: LineSegment StartX=-14.1386 StartY=-3.3581 StartZ=0 EndX=-13.8673 EndY=-3.55064 EndZ=0
    g2: LineSegment StartX=-10.8098 StartY=-4.00788 StartZ=0 EndX=-10.5716 EndY=-4.29909 EndZ=0
    g3: LineSegment StartX=-10.5716 StartY=-4.29909 StartZ=0 EndX=-10.1338 EndY=-4.33136 EndZ=0
    g4: LineSegment StartX=-10.1338 StartY=-4.33136 StartZ=0 EndX=-9.89036 EndY=-4.3898 EndZ=0
    g5: LineSegment StartX=-9.51656 StartY=-5.73022 StartZ=0 EndX=-9.24931 EndY=-5.76229 EndZ=0
    g6: LineSegment StartX=-9.24931 StartY=-5.76229 StartZ=0 EndX=-8.92861 EndY=-5.90126 EndZ=0
    g7: LineSegment StartX=-8.92861 StartY=-5.90126 StartZ=0 EndX=-8.54378 EndY=-5.86384 EndZ=0
    g8: LineSegment StartX=-8.54378 StartY=-5.86384 StartZ=0 EndX=-7.71788 EndY=-5.75845 EndZ=0
    g9: LineSegment StartX=-7.71788 StartY=-5.75845 StartZ=0 EndX=-7.37291 EndY=-5.97257 EndZ=0
    g10: LineSegment StartX=-7.37291 StartY=-5.97257 StartZ=0 EndX=-6.72487 EndY=-5.72038 EndZ=0
    g11: LineSegment StartX=-6.72487 StartY=-5.72038 StartZ=0 EndX=-6.27066 EndY=-5.69481 EndZ=0
    g12: LineSegment StartX=-6.27066 StartY=-5.69481 StartZ=0 EndX=-6.06223 EndY=-5.80493 EndZ=0
    g13: LineSegment StartX=-6.06223 StartY=-5.80493 StartZ=0 EndX=-5.35089 EndY=-5.48914 EndZ=0
    g14: LineSegment StartX=-5.35089 StartY=-5.48914 StartZ=0 EndX=-5.02402 EndY=-5.48914 EndZ=0
    g15: LineSegment StartX=-5.02402 StartY=-5.48914 StartZ=0 EndX=-4.80126 EndY=-5.53132 EndZ=0
    g16: LineSegment StartX=-4.80126 StartY=-5.53132 StartZ=0 EndX=-4.19735 EndY=-5.16248 EndZ=0
    g17: LineSegment StartX=-3.75191 StartY=-4.97251 StartZ=0 EndX=-3.37714 EndY=-4.97251 EndZ=0
    g18: LineSegment StartX=-3.37714 StartY=-4.97251 StartZ=0 EndX=-2.81898 EndY=-4.45422 EndZ=0
    g19: LineSegment StartX=-2.81898 StartY=-4.45422 StartZ=0 EndX=-2.62761 EndY=-4.34259 EndZ=0
    g20: LineSegment StartX=-2.62761 StartY=-4.34259 StartZ=0 EndX=-2.15112 EndY=-4.35765 EndZ=0
    g21: LineSegment StartX=-2.38042 StartY=-4.51801 StartZ=0 EndX=-3.18577 EndY=-5.42702 EndZ=0
    g22: LineSegment StartX=-3.18577 StartY=-5.42702 StartZ=0 EndX=-3.61318 EndY=-6.05824 EndZ=0
    g23: LineSegment StartX=-3.61318 StartY=-6.05824 StartZ=0 EndX=-3.7111 EndY=-6.64579 EndZ=0
    g24: LineSegment StartX=-3.7111 StartY=-6.64579 StartZ=0 EndX=-3.83514 EndY=-7.15501 EndZ=0
    g25: LineSegment StartX=-3.83514 StartY=-7.15501 StartZ=0 EndX=-3.75878 EndY=-7.50876 EndZ=0
    g26: LineSegment StartX=-3.75878 StartY=-7.50876 StartZ=0 EndX=-3.70596 EndY=-7.68135 EndZ=0
    g27: LineSegment StartX=-3.70596 StartY=-7.68135 StartZ=0 EndX=-3.53967 EndY=-7.85202 EndZ=0
    g28: LineSegment StartX=-3.53967 StartY=-7.85202 StartZ=0 EndX=-3.4685 EndY=-8.65617 EndZ=0
    g29: LineSegment StartX=-3.27268 StartY=-8.56671 StartZ=0 EndX=-3.16823 EndY=-8.76909 EndZ=0
    g30: LineSegment StartX=-3.07088 StartY=-9.32083 StartZ=0 EndX=-2.84207 EndY=-9.3355 EndZ=0
    g31: LineSegment StartX=-2.84207 StartY=-9.3355 StartZ=0 EndX=-2.45193 EndY=-10.0982 EndZ=0
    g32: LineSegment StartX=-2.45193 StartY=-10.0982 StartZ=0 EndX=-2.24953 EndY=-10.1304 EndZ=0
    g33: LineSegment StartX=-2.24953 StartY=-10.1304 StartZ=0 EndX=-0.96042 EndY=-11.8753 EndZ=0
    g34: LineSegment StartX=-0.96042 StartY=-11.8753 StartZ=0 EndX=-0.153326 EndY=-11.3889 EndZ=0
    g35: LineSegment StartX=-0.153326 StartY=-11.3889 StartZ=0 EndX=0.461347 EndY=-10.7689 EndZ=0
    g36: LineSegment StartX=0.461347 StartY=-10.7689 StartZ=0 EndX=0.669802 EndY=-10.7261 EndZ=0
    g37: LineSegment StartX=0.669802 StartY=-10.7261 StartZ=0 EndX=1.31724 EndY=-9.70998 EndZ=0
    g38: LineSegment StartX=1.31724 StartY=-9.70998 StartZ=0 EndX=1.51826 EndY=-9.65081 EndZ=0
    g39: LineSegment StartX=1.51826 StartY=-9.65081 StartZ=0 EndX=1.74022 EndY=-9.08937 EndZ=0
    g40: LineSegment StartX=1.74022 StartY=-9.08937 StartZ=0 EndX=2.02094 EndY=-9.04367 EndZ=0
    g41: LineSegment StartX=2.02094 StartY=-9.04367 StartZ=0 EndX=2.39306 EndY=-7.80327 EndZ=0
    g42: LineSegment StartX=2.39306 StartY=-7.80327 StartZ=0 EndX=2.58839 EndY=-7.69871 EndZ=0
    g43: LineSegment StartX=2.6542 StartY=-7.03945 StartZ=0 EndX=2.86963 EndY=-6.81749 EndZ=0
    g44: LineSegment StartX=2.86963 StartY=-6.81749 StartZ=0 EndX=3.0916 EndY=-6.92847 EndZ=0
    g45: LineSegment StartX=3.0916 StartY=-6.92847 StartZ=0 EndX=3.79666 EndY=-7.57478 EndZ=0
    g46: LineSegment StartX=3.79666 StartY=-7.57478 StartZ=0 EndX=3.93376 EndY=-7.50297 EndZ=0
    g47: LineSegment StartX=3.93376 StartY=-7.50297 StartZ=0 EndX=4.46256 EndY=-7.97301 EndZ=0
    g48: LineSegment StartX=4.46256 StartY=-7.97301 StartZ=0 EndX=4.68452 EndY=-7.92079 EndZ=0
    g49: LineSegment StartX=4.68452 StartY=-7.92079 StartZ=0 EndX=5.1154 EndY=-8.34513 EndZ=0
    g50: LineSegment StartX=5.1154 StartY=-8.34513 StartZ=0 EndX=5.32431 EndY=-8.28637 EndZ=0
    g51: LineSegment StartX=5.32431 StartY=-8.28637 StartZ=0 EndX=6.23668 EndY=-8.79564 EndZ=0
    g52: LineSegment StartX=6.23668 StartY=-8.79564 StartZ=0 EndX=6.50362 EndY=-8.76631 EndZ=0
    g53: LineSegment StartX=6.50362 StartY=-8.76631 StartZ=0 EndX=7.14802 EndY=-9.05537 EndZ=0
    g54: LineSegment StartX=7.14802 StartY=-9.05537 StartZ=0 EndX=8.04883 EndY=-9.18613 EndZ=0
    g55: LineSegment StartX=8.04883 StartY=-9.18613 StartZ=0 EndX=8.36847 EndY=-7.93662 EndZ=0
    g56: LineSegment StartX=8.36847 StartY=-7.93662 StartZ=0 EndX=8.49923 EndY=-7.79133 EndZ=0
    g57: LineSegment StartX=8.49923 StartY=-7.79133 StartZ=0 EndX=8.43477 EndY=-6.72206 EndZ=0
    g58: LineSegment StartX=8.43477 StartY=-6.72206 StartZ=0 EndX=8.58621 EndY=-6.47988 EndZ=0
    g59: LineSegment StartX=8.58621 StartY=-6.47988 StartZ=0 EndX=8.32296 EndY=-5.53178 EndZ=0
    g60: LineSegment StartX=8.32296 StartY=-5.53178 StartZ=0 EndX=8.43984 EndY=-5.19091 EndZ=0
    g61: LineSegment StartX=8.43984 StartY=-5.19091 StartZ=0 EndX=8.07426 EndY=-4.39307 EndZ=0
    g62: LineSegment StartX=8.07426 StartY=-4.39307 StartZ=0 EndX=8.04236 EndY=-4.17777 EndZ=0
    g63: LineSegment StartX=8.04236 StartY=-4.17777 StartZ=0 EndX=8.0902 EndY=-3.99438 EndZ=0
    g64: LineSegment StartX=8.4103 StartY=-4.11103 StartZ=0 EndX=8.72013 EndY=-4.0502 EndZ=0
    g65: LineSegment StartX=8.72013 StartY=-4.0502 StartZ=0 EndX=9.31817 EndY=-4.0502 EndZ=0
    g66: LineSegment StartX=9.31817 StartY=-4.0502 StartZ=0 EndX=9.82964 EndY=-4.15887 EndZ=0
    g67: LineSegment StartX=10.1326 StartY=-3.9675 StartZ=0 EndX=10.5175 EndY=-3.9623 EndZ=0
    g68: LineSegment StartX=10.5175 StartY=-3.9623 StartZ=0 EndX=10.8831 EndY=-3.97536 EndZ=0
    g69: LineSegment StartX=10.8831 StartY=-3.97536 StartZ=0 EndX=11.2245 EndY=-4.09431 EndZ=0
    g70: LineSegment StartX=11.2245 StartY=-4.09431 StartZ=0 EndX=11.6861 EndY=-3.91007 EndZ=0
    g71: LineSegment StartX=11.6861 StartY=-3.91007 StartZ=0 EndX=12.1039 EndY=-3.88396 EndZ=0
    g72: LineSegment StartX=12.1039 StartY=-3.88396 StartZ=0 EndX=12.6 EndY=-3.9623 EndZ=0
    g73: LineSegment StartX=12.6 StartY=-3.9623 StartZ=0 EndX=13.5793 EndY=-3.87743 EndZ=0
    g74: LineSegment StartX=13.5793 StartY=-3.87743 StartZ=0 EndX=14.3888 EndY=-3.74687 EndZ=0
    g75: LineSegment StartX=14.3888 StartY=-3.74687 StartZ=0 EndX=14.7544 EndY=-3.68158 EndZ=0
    g76: LineSegment StartX=14.7544 StartY=-3.68158 StartZ=0 EndX=15.2767 EndY=-3.75339 EndZ=0
    g77: LineSegment StartX=15.2767 StartY=-3.75339 StartZ=0 EndX=15.0432 EndY=-3.24137 EndZ=0
    g78: LineSegment StartX=15.0432 StartY=-3.24137 StartZ=0 EndX=14.5209 EndY=-2.51672 EndZ=0
    g79: LineSegment StartX=14.5209 StartY=-2.51672 StartZ=0 EndX=14.0378 EndY=-1.99445 EndZ=0
    g80: LineSegment StartX=14.0378 StartY=-1.99445 StartZ=0 EndX=13.2802 EndY=-1.54625 EndZ=0
    g81: LineSegment StartX=13.2802 StartY=-1.54625 StartZ=0 EndX=13.0438 EndY=-1.23117 EndZ=0
    g82: LineSegment StartX=13.0438 StartY=-1.23117 StartZ=0 EndX=12.1074 EndY=-0.797939 EndZ=0
    g83: LineSegment StartX=12.1074 StartY=-0.797939 StartZ=0 EndX=11.3804 EndY=-0.250878 EndZ=0
    g84: LineSegment StartX=11.3804 StartY=-0.250878 StartZ=0 EndX=10.4396 EndY=0.304889 EndZ=0
    g85: LineSegment StartX=10.4396 StartY=0.304889 StartZ=0 EndX=9.59526 EndY=0.727998 EndZ=0
    g86: LineSegment StartX=9.59526 StartY=0.727998 StartZ=0 EndX=8.53624 EndY=0.97306 EndZ=0
    g87: LineSegment StartX=8.53624 StartY=0.97306 StartZ=0 EndX=7.199 EndY=0.97306 EndZ=0
    g88: LineSegment StartX=7.199 StartY=0.97306 StartZ=0 EndX=5.77932 EndY=0.795578 EndZ=0
    g89: LineSegment StartX=5.77932 StartY=0.795578 StartZ=0 EndX=5.60186 EndY=0.795578 EndZ=0
    g90: LineSegment StartX=5.60186 StartY=0.795578 StartZ=0 EndX=5.83178 EndY=0.981815 EndZ=0
    g91: LineSegment StartX=5.83178 StartY=0.981815 StartZ=0 EndX=6.25403 EndY=1.1582 EndZ=0
    g92: LineSegment StartX=6.30214 StartY=1.38269 StartZ=0 EndX=7.17987 EndY=1.70686 EndZ=0
    g93: LineSegment StartX=7.17987 StartY=1.70686 StartZ=0 EndX=7.44682 EndY=1.79438 EndZ=0
    g94: LineSegment StartX=7.44682 StartY=1.79438 StartZ=0 EndX=7.49058 EndY=2.12696 EndZ=0
    g95: LineSegment StartX=7.49058 StartY=2.12696 StartZ=0 EndX=8.30058 EndY=2.66839 EndZ=0
    g96: LineSegment StartX=8.30058 StartY=2.66839 StartZ=0 EndX=8.68575 EndY=2.81854 EndZ=0
    g97: LineSegment StartX=8.68575 StartY=2.81854 StartZ=0 EndX=8.68575 EndY=3.12537 EndZ=0
    g98: LineSegment StartX=8.68575 StartY=3.12537 StartZ=0 EndX=8.89508 EndY=3.18684 EndZ=0
    g99: LineSegment StartX=8.89508 StartY=3.18684 StartZ=0 EndX=9.63492 EndY=4.06602 EndZ=0
    g100: LineSegment StartX=9.63492 StartY=4.06602 StartZ=0 EndX=9.62638 EndY=4.32743 EndZ=0
    g101: LineSegment StartX=9.62638 StartY=4.32743 StartZ=0 EndX=10.2068 EndY=5.18314 EndZ=0
    g102: LineSegment StartX=10.2068 StartY=5.18314 StartZ=0 EndX=9.25518 EndY=5.64445 EndZ=0
    g103: LineSegment StartX=9.1102 StartY=5.87597 StartZ=0 EndX=8.32132 EndY=5.97336 EndZ=0
    g104: LineSegment StartX=8.32132 StartY=5.97336 StartZ=0 EndX=8.15466 EndY=6.06625 EndZ=0
    g105: LineSegment StartX=7.63471 StartY=6.13088 StartZ=0 EndX=7.56391 EndY=6.33267 EndZ=0
    g106: LineSegment StartX=7.56391 StartY=6.33267 StartZ=0 EndX=6.74832 EndY=6.35496 EndZ=0
    g107: LineSegment StartX=6.74832 StartY=6.35496 StartZ=0 EndX=6.46819 EndY=6.29526 EndZ=0
    g108: LineSegment StartX=6.46819 StartY=6.29526 StartZ=0 EndX=6.27042 EndY=6.61061 EndZ=0
    g109: LineSegment StartX=6.27042 StartY=6.61061 StartZ=0 EndX=5.40453 EndY=6.33267 EndZ=0
    g110: LineSegment StartX=5.40453 StartY=6.33267 StartZ=0 EndX=5.27091 EndY=6.47164 EndZ=0
    g111: LineSegment StartX=5.27091 StartY=6.47164 StartZ=0 EndX=4.56942 EndY=6.24725 EndZ=0
    g112: LineSegment StartX=4.56942 StartY=6.24725 StartZ=0 EndX=4.44161 EndY=6.40652 EndZ=0
    g113: LineSegment StartX=4.44161 StartY=6.40652 StartZ=0 EndX=3.4195 EndY=5.94588 EndZ=0
    g114: LineSegment StartX=3.4195 StartY=5.94588 StartZ=0 EndX=3.29192 EndY=6.1532 EndZ=0
    g115: LineSegment StartX=3.29192 StartY=6.1532 StartZ=0 EndX=2.15964 EndY=5.49137 EndZ=0
    g116: LineSegment StartX=2.15964 StartY=5.49137 StartZ=0 EndX=2.00016 EndY=5.69869 EndZ=0
    g117: LineSegment StartX=2.00016 StartY=5.69869 StartZ=0 EndX=1.6185 EndY=5.34828 EndZ=0
    g118: LineSegment StartX=1.6185 StartY=5.34828 StartZ=0 EndX=1.45984 EndY=5.94974 EndZ=0
    g119: LineSegment StartX=1.38165 StartY=6.28651 StartZ=0 EndX=1.14534 EndY=6.29963 EndZ=0
    g120: LineSegment StartX=0.348522 StartY=7.29544 StartZ=0 EndX=0.126706 EndY=7.68126 EndZ=0
    g121: LineSegment StartX=0.126706 StartY=7.68126 StartZ=0 EndX=-0.415308 EndY=8.18163 EndZ=0
    g122: LineSegment StartX=-0.415308 StartY=8.18163 StartZ=0 EndX=-0.872658 EndY=8.6237 EndZ=0
    g123: LineSegment StartX=-0.872658 StartY=8.6237 StartZ=0 EndX=-1.12074 EndY=8.64329 EndZ=0
    g124: LineSegment StartX=-1.12074 StartY=8.64329 StartZ=0 EndX=-1.79316 EndY=9.11986 EndZ=0
    g125: LineSegment StartX=-1.79316 StartY=9.11986 StartZ=0 EndX=-2.31488 EndY=9.12122 EndZ=0
    g126: LineSegment StartX=-2.31488 StartY=9.12122 StartZ=0 EndX=-2.71321 EndY=9.13846 EndZ=0
    g127: LineSegment StartX=-2.71321 StartY=9.13846 StartZ=0 EndX=-2.88425 EndY=9.34157 EndZ=0
    g128: LineSegment StartX=-2.88425 StartY=9.34157 StartZ=0 EndX=-3.16779 EndY=9.26454 EndZ=0
    g129: LineSegment StartX=-3.70739 StartY=9.82796 StartZ=0 EndX=-4.04915 EndY=9.7003 EndZ=0
    g130: LineSegment StartX=-4.04915 StartY=9.7003 StartZ=0 EndX=-4.42988 EndY=10.011 EndZ=0
    g131: LineSegment StartX=-5.98947 StartY=10.3656 StartZ=0 EndX=-7.32605 EndY=10.4108 EndZ=0
    g132: LineSegment StartX=-7.25254 StartY=9.13254 StartZ=0 EndX=-7.36878 EndY=8.7693 EndZ=0
    g133: LineSegment StartX=-7.36878 StartY=8.7693 StartZ=0 EndX=-7.2614 EndY=7.83762 EndZ=0
    g134: LineSegment StartX=-7.2614 StartY=7.83762 StartZ=0 EndX=-7.41112 EndY=7.6042 EndZ=0
    g135: LineSegment StartX=-7.41112 StartY=7.6042 StartZ=0 EndX=-7.09216 EndY=6.74302 EndZ=0
    g136: LineSegment StartX=-7.09216 StartY=6.74302 StartZ=0 EndX=-7.10014 EndY=6.55962 EndZ=0
    g137: LineSegment StartX=-7.10014 StartY=6.55962 StartZ=0 EndX=-7.29151 EndY=6.3842 EndZ=0
    g138: LineSegment StartX=-7.29151 StartY=6.3842 StartZ=0 EndX=-6.74132 EndY=5.29976 EndZ=0
    g139: LineSegment StartX=-6.74132 StartY=5.29976 StartZ=0 EndX=-6.87495 EndY=5.02732 EndZ=0
    g140: LineSegment StartX=-6.87495 StartY=5.02732 StartZ=0 EndX=-6.31586 EndY=4.42065 EndZ=0
    g141: LineSegment StartX=-6.31586 StartY=4.42065 StartZ=0 EndX=-6.30396 EndY=4.19463 EndZ=0
    g142: LineSegment StartX=-6.30396 StartY=4.19463 StartZ=0 EndX=-6.05415 EndY=4.0043 EndZ=0
    g143: LineSegment StartX=-6.05415 StartY=4.0043 StartZ=0 EndX=-6.18501 EndY=3.95672 EndZ=0
    g144: LineSegment StartX=-6.18501 StartY=3.95672 StartZ=0 EndX=-5.54265 EndY=3.07645 EndZ=0
    g145: LineSegment StartX=-5.54265 StartY=3.07645 StartZ=0 EndX=-5.57833 EndY=2.90991 EndZ=0
    g146: LineSegment StartX=-5.57833 StartY=2.90991 StartZ=0 EndX=-5.1263 EndY=2.41029 EndZ=0
    g147: LineSegment StartX=-5.1263 StartY=2.41029 StartZ=0 EndX=-5.18578 EndY=2.26755 EndZ=0
    g148: LineSegment StartX=-5.18578 StartY=2.26755 StartZ=0 EndX=-4.73375 EndY=1.89878 EndZ=0
    g149: LineSegment StartX=-4.73375 StartY=1.89878 StartZ=0 EndX=-4.42446 EndY=1.5895 EndZ=0
    g150: LineSegment StartX=-4.42446 StartY=1.5895 StartZ=0 EndX=-5.31663 EndY=1.29211 EndZ=0
    g151: LineSegment StartX=-5.31663 StartY=1.29211 StartZ=0 EndX=-5.84004 EndY=1.08988 EndZ=0
    g152: LineSegment StartX=-5.84004 StartY=1.08988 StartZ=0 EndX=-6.04226 EndY=0.792495 EndZ=0
    g153: LineSegment StartX=-6.04226 StartY=0.792495 StartZ=0 EndX=-6.94632 EndY=0.994719 EndZ=0
    g154: LineSegment StartX=-6.94632 StartY=0.994719 StartZ=0 EndX=-7.19613 EndY=0.887659 EndZ=0
    g155: LineSegment StartX=-7.19613 StartY=0.887659 StartZ=0 EndX=-7.8147 EndY=1.0423 EndZ=0
    g156: LineSegment StartX=-7.8147 StartY=1.0423 StartZ=0 EndX=-8.02502 EndY=0.969153 EndZ=0
    g157: LineSegment StartX=-8.02502 StartY=0.969153 StartZ=0 EndX=-8.60267 EndY=1.03042 EndZ=0
    g158: LineSegment StartX=-8.60267 StartY=1.03042 StartZ=0 EndX=-8.8346 EndY=0.872878 EndZ=0
    g159: LineSegment StartX=-8.8346 StartY=0.872878 StartZ=0 EndX=-9.33349 EndY=0.929767 EndZ=0
    g160: LineSegment StartX=-9.33349 StartY=0.929767 StartZ=0 EndX=-9.66169 EndY=0.649695 EndZ=0
    g161: LineSegment StartX=-9.66169 StartY=0.649695 StartZ=0 EndX=-10.3249 EndY=0.649695 EndZ=0
    g162: LineSegment StartX=-10.3249 StartY=0.649695 StartZ=0 EndX=-11.0107 EndY=0.32425 EndZ=0
    g163: LineSegment StartX=-11.0107 StartY=0.32425 StartZ=0 EndX=-11.7283 EndY=0.053139 EndZ=0
    g164: LineSegment StartX=-11.7283 StartY=0.053139 StartZ=0 EndX=-12.2971 EndY=-0.13161 EndZ=0
    g165: LineSegment StartX=-12.2971 StartY=-0.13161 StartZ=0 EndX=-12.4212 EndY=-0.347049 EndZ=0
    g166: LineSegment StartX=-12.4212 StartY=-0.347049 StartZ=0 EndX=-13.296 EndY=-0.817096 EndZ=0
    g167: LineSegment StartX=-13.296 StartY=-0.817096 StartZ=0 EndX=-13.9227 EndY=-1.24144 EndZ=0
    g168: LineSegment StartX=-13.9227 StartY=-1.24144 StartZ=0 EndX=-14.1708 EndY=-1.59398 EndZ=0
    g169: LineSegment StartX=-14.1708 StartY=-1.59398 StartZ=0 EndX=-14.5386 EndY=-2.09216 EndZ=0
    g170: LineSegment StartX=-14.5386 StartY=-2.09216 StartZ=0 EndX=-14.7831 EndY=-2.4577 EndZ=0
    g171: LineSegment StartX=-14.7831 StartY=-2.4577 StartZ=0 EndX=-15.0667 EndY=-2.9879 EndZ=0
    g172: LineSegment StartX=7.82861 StartY=6.04487 StartZ=0 EndX=7.63471 EndY=6.13088 EndZ=0
    g173: LineSegment StartX=-14.4175 StartY=-3.20194 StartZ=0 EndX=-14.1386 EndY=-3.3581 EndZ=0
    g174: LineSegment StartX=-13.8673 StartY=-3.55064 StartZ=0 EndX=-13.4107 EndY=-3.57136 EndZ=0
    g175: LineSegment StartX=-13.1321 StartY=-3.61699 StartZ=0 EndX=-12.817 EndY=-3.62343 EndZ=0
    g176: LineSegment StartX=-12.817 StartY=-3.62343 StartZ=0 EndX=-12.4662 EndY=-3.85302 EndZ=0
    g177: LineSegment StartX=-13.4107 StartY=-3.57136 StartZ=0 EndX=-13.1321 EndY=-3.61699 EndZ=0
    g178: LineSegment StartX=-12.4662 StartY=-3.85302 StartZ=0 EndX=-11.8704 EndY=-3.85302 EndZ=0
    g179: LineSegment StartX=-11.8704 StartY=-3.85302 StartZ=0 EndX=-11.5204 EndY=-4.00836 EndZ=0
    g180: LineSegment StartX=-11.5204 StartY=-4.00836 StartZ=0 EndX=-11.1389 EndY=-4.05555 EndZ=0
    g181: LineSegment StartX=-11.1389 StartY=-4.05555 StartZ=0 EndX=-10.8098 EndY=-4.00788 EndZ=0
    g182: LineSegment StartX=-9.89036 StartY=-4.3898 StartZ=0 EndX=-9.99555 EndY=-4.87697 EndZ=0
    g183: LineSegment StartX=-9.99555 StartY=-4.87697 StartZ=0 EndX=-10.0894 EndY=-5.36391 EndZ=0
    g184: LineSegment StartX=-10.0894 StartY=-5.36391 StartZ=0 EndX=-10.107 EndY=-5.50471 EndZ=0
    g185: LineSegment StartX=-10.107 StartY=-5.50471 StartZ=0 EndX=-9.77848 EndY=-5.63965 EndZ=0
    g186: LineSegment StartX=-9.77848 StartY=-5.63965 StartZ=0 EndX=-9.51656 EndY=-5.73022 EndZ=0
    g187: LineSegment StartX=-4.19735 StartY=-5.16248 StartZ=0 EndX=-3.75191 EndY=-4.97251 EndZ=0
    g188: LineSegment StartX=-2.38042 StartY=-4.51801 StartZ=0 EndX=-2.15112 EndY=-4.35765 EndZ=0
    g189: LineSegment StartX=-3.4685 StartY=-8.65617 StartZ=0 EndX=-3.27268 EndY=-8.56671 EndZ=0
    g190: LineSegment StartX=-3.16823 StartY=-8.76909 StartZ=0 EndX=-3.07088 EndY=-9.32083 EndZ=0
    g191: LineSegment StartX=2.58839 StartY=-7.69871 StartZ=0 EndX=2.6542 EndY=-7.03945 EndZ=0
    g192: LineSegment StartX=8.0902 StartY=-3.99438 StartZ=0 EndX=8.4103 EndY=-4.11103 EndZ=0
    g193: LineSegment StartX=9.82964 StartY=-4.15887 StartZ=0 EndX=10.1326 EndY=-3.9675 EndZ=0
    g194: LineSegment StartX=6.30214 StartY=1.38269 StartZ=0 EndX=6.25403 EndY=1.1582 EndZ=0
    g195: LineSegment StartX=1.38165 StartY=6.28651 StartZ=0 EndX=1.45984 EndY=5.94974 EndZ=0
    g196: LineSegment StartX=0.348522 StartY=7.29544 StartZ=0 EndX=0.824344 EndY=6.91479 EndZ=0
    g197: LineSegment StartX=0.824344 StartY=6.91479 StartZ=0 EndX=1.14534 EndY=6.29963 EndZ=0
    g198: LineSegment StartX=-3.70739 StartY=9.82796 StartZ=0 EndX=-3.16779 EndY=9.26454 EndZ=0
    g199: LineSegment StartX=-5.98947 StartY=10.3656 StartZ=0 EndX=-5.43038 EndY=10.4489 EndZ=0
    g200: LineSegment StartX=-5.43038 StartY=10.4489 StartZ=0 EndX=-4.9791 EndY=10.1425 EndZ=0
    g201: LineSegment StartX=-4.42988 StartY=10.011 StartZ=0 EndX=-4.9791 EndY=10.1425 EndZ=0
    g202: LineSegment StartX=-7.25254 StartY=9.13254 StartZ=0 EndX=-7.32605 EndY=10.4108 EndZ=0
    g203: LineSegment StartX=7.82861 StartY=6.04487 StartZ=0 EndX=8.15466 EndY=6.06625 EndZ=0
    g204: LineSegment StartX=9.1102 StartY=5.87597 StartZ=0 EndX=9.25518 EndY=5.64445 EndZ=0
  constraints (114):
    c: Coincident(g4,g3)
    c: Coincident(g6,g5)
    c: Coincident(g8,g7)
    c: Coincident(g9,g8)
    c: Coincident(g10,g9)
    c: Coincident(g11,g10)
    c: Coincident(g13,g12)
    c: Coincident(g16,g15)
    c: Coincident(g22,g21)
    c: Coincident(g25,g24)
    c: Coincident(g26,g25)
    c: Coincident(g28,g27)
    c: Coincident(g33,g32)
    c: Coincident(g37,g36)
    c: Coincident(g38,g37)
    c: Coincident(g40,g39)
    c: Coincident(g44,g43)
    c: Coincident(g51,g50)
    c: Coincident(g52,g51)
    c: Coincident(g57,g56)
    c: Coincident(g58,g57)
    c: Coincident(g59,g58)
    c: Coincident(g61,g60)
    c: Coincident(g63,g62)
    c: Coincident(g66,g65)
    c: Coincident(g70,g69)
    c: Coincident(g72,g71)
    c: Coincident(g73,g72)
    c: Coincident(g74,g73)
    c: Coincident(g77,g76)
    c: Coincident(g80,g79)
    c: Coincident(g81,g80)
    c: Coincident(g83,g82)
    c: Coincident(g85,g84)
    c: Coincident(g86,g85)
    c: Coincident(g87,g86)
    c: Coincident(g89,g88)
    c: Coincident(g90,g89)
    c: Coincident(g91,g90)
    c: Coincident(g93,g92)
    c: Coincident(g95,g94)
    c: Coincident(g97,g96)
    c: Coincident(g98,g97)
    c: Coincident(g99,g98)
    c: Coincident(g100,g99)
    c: Coincident(g104,g103)
    c: Coincident(g106,g105)
    c: Coincident(g107,g106)
    c: Coincident(g111,g110)
    c: Coincident(g113,g112)
    c: Coincident(g118,g117)
    c: Coincident(g122,g121)
    c: Coincident(g126,g125)
    c: Coincident(g130,g129)
    c: Coincident(g133,g132)
    c: Coincident(g134,g133)
    c: Coincident(g135,g134)
    c: Coincident(g139,g138)
    c: Coincident(g142,g141)
    c: Coincident(g156,g155)
    c: Coincident(g157,g156)
    c: Coincident(g159,g158)
    c: Coincident(g161,g160)
    c: Coincident(g164,g163)
    c: Coincident(g165,g164)
    c: Coincident(g168,g167)
    c: Coincident(g169,g168)
    c: Coincident(g171,g170)
    c: Coincident(g171,g0)
    c: Coincident(g172,g105)
    c: DistanceX(g165) = -12.4212
    c: DistanceY(g165) = -0.347049
    c: Coincident(g173,g0)
    c: Coincident(g173,g1)
    c: Coincident(g174,g1)
    c: Coincident(g177,g174)
    c: Coincident(g177,g175)
    c: Coincident(g178,g176)
    c: Coincident(g181,g2)
    c: Coincident(g182,g4)
    c: Coincident(g186,g185)
    c: Coincident(g186,g5)
    c: Coincident(g187,g16)
    c: Coincident(g187,g17)
    c: Coincident(g188,g21)
    c: Coincident(g188,g20)
    c: Coincident(g189,g28)
    c: Coincident(g189,g29)
    c: Coincident(g190,g29)
    c: Coincident(g190,g30)
    c: Coincident(g191,g42)
    c: Coincident(g191,g43)
    c: Coincident(g192,g63)
    c: Coincident(g192,g64)
    c: Coincident(g193,g66)
    c: Coincident(g193,g67)
    c: Coincident(g194,g92)
    c: Coincident(g194,g91)
    c: Coincident(g195,g119)
    c: Coincident(g195,g118)
    c: Coincident(g196,g120)
    c: Coincident(g197,g119)
    c: Coincident(g198,g129)
    c: Coincident(g198,g128)
    c: Coincident(g199,g131)
    c: Coincident(g200,g199)
    c: Coincident(g201,g130)
    c: Coincident(g201,g200)
    c: Coincident(g202,g132)
    c: Coincident(g202,g131)
    c: Coincident(g203,g172)
    c: Coincident(g203,g104)
    c: Coincident(g204,g103)
    c: Coincident(g204,g102)
FEATURE [PartDesign::Pad] Pad002
  Direction = (0,0,1)
  Length = 3
  Length2 = 10
  Profile = -> Sketch002
  ReferenceAxis = -> Sketch002 [N_Axis]
  Type = 0
FEATURE [PartDesign::Body] Body002  label="logo004"
  Group = -> [Sketch002,Pad002]
  Origin = -> Origin002
  Placement = pos=(39.35,-43,30) rot=(1,0,0;1.5708rad)
  Tip = -> Pad002
FEATURE [Part::MultiFuse] Fusion041  label="logo005"
  Placement = pos=(-69,-26,58) rot=(1,0,0;3.14159rad)
  Shapes = -> [Body002,Box069]
